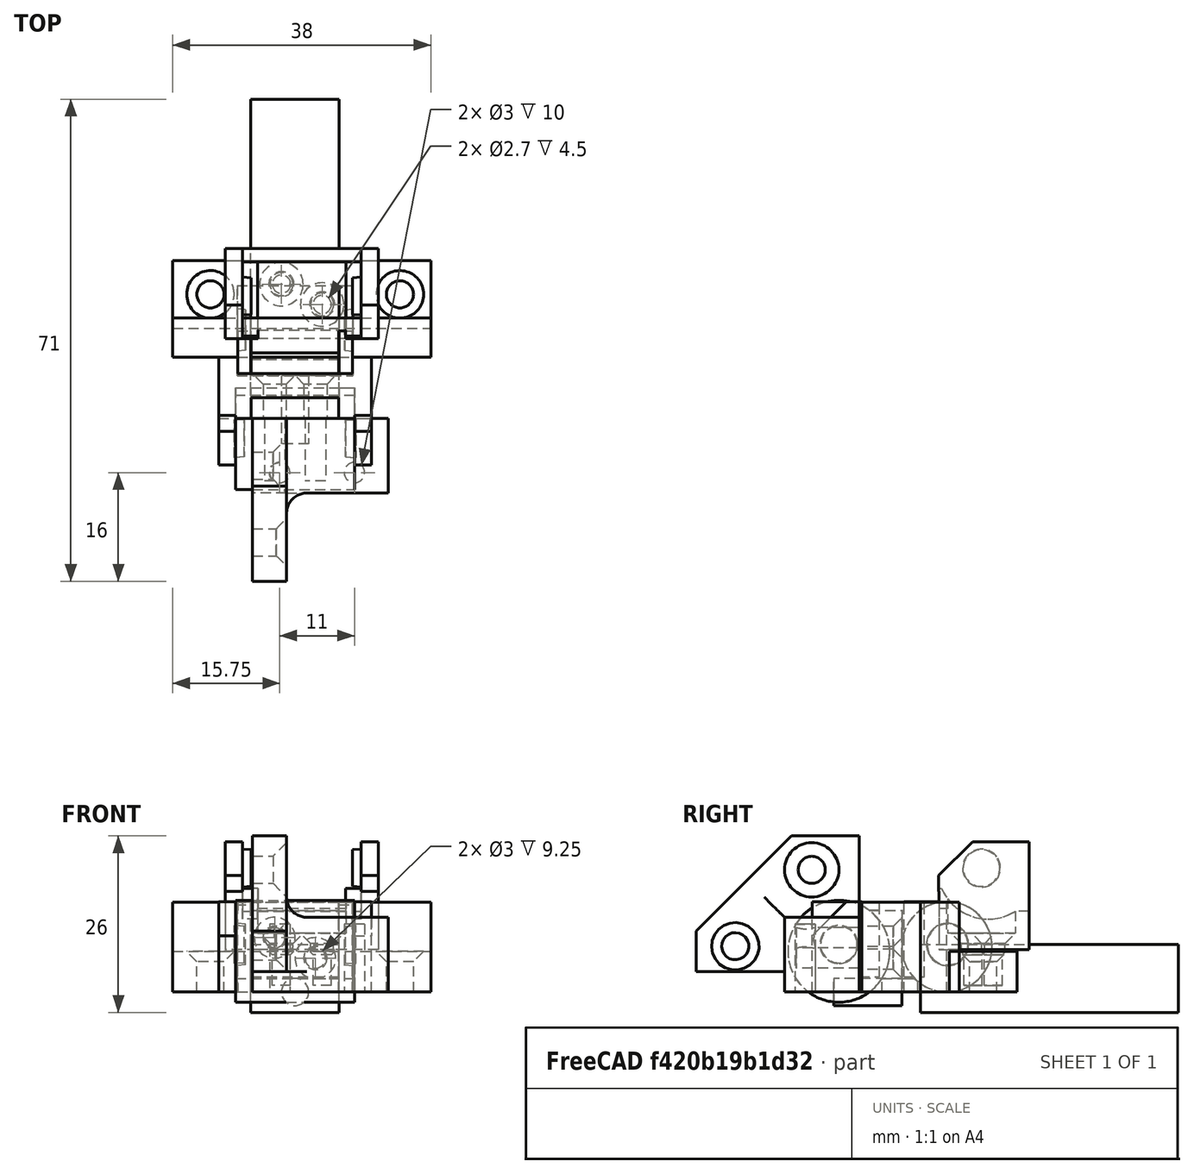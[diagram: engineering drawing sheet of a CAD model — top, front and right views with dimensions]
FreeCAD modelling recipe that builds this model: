
FCSTD DOCUMENT  (FreeCAD 0.18R16146 (Git))
Label: Cable Chain 0.1
License: All rights reserved
LicenseURL: http://en.wikipedia.org/wiki/All_rights_reserved
objects: Part::Box×39, Part::MultiFuse×31, Part::Cut×22, Part::Cylinder×21, Part::Cone×12, Part::Chamfer×9, Part::Mirroring×6, Part::Fuse×3, Mesh::Feature×2, Part::Fillet×2, App::DocumentObjectGroup×1
note: 145 computed .brp shape members not serialized (recipe doc carries the construction recipe); baked Part::Feature solids carry a one-line shape summary decoded from their .brp

FEATURE [Mesh::Feature] CableChain  label="Original STL From Thingiverse"
FEATURE [Part::Box] Box  label="Main Body"
  AttacherType = Attacher::AttachEngine3D
  Height = 13.25
  Length = 22.5
  Placement = pos=(-11.25,-6.25,0) rot=(0,0,1;0rad)
  Width = 9
FEATURE [Part::Cylinder] Cylinder  label="Bump Cylinder"
  Angle = 360
  AttacherType = Attacher::AttachEngine3D
  Height = 17.5
  Placement = pos=(-8.75,-9.25,6) rot=(0,1,0;1.5708rad)
  Radius = 7.5
FEATURE [Part::Cylinder] Cylinder001  label="Dent Cylinder"
  Angle = 360
  AttacherType = Attacher::AttachEngine3D
  Height = 17
  Placement = pos=(-8.5,6.65,6.65) rot=(0,1,0;1.5708rad)
  Radius = 6.65
FEATURE [Part::Box] Box001  label="Cube001"
  AttacherType = Attacher::AttachEngine3D
  Height = 13.3
  Length = 2
  Placement = pos=(6.45,0.35,0) rot=(0,0,1;0rad)
  Width = 6.3
FEATURE [Part::Cone] Cone
  Angle = 360
  AttacherType = Attacher::AttachEngine3D
  Height = 1.2
  Placement = pos=(7.3,6.75,7) rot=(0,1,0;1.5708rad)
  Radius1 = 3
  Radius2 = 3.1
FEATURE [Part::Box] Box002  label="Cube002"
  AttacherType = Attacher::AttachEngine3D
  Height = 13.3
  Length = 2
  Placement = pos=(-8.45,0.35,0) rot=(0,0,1;0rad)
  Width = 6.3
FEATURE [Part::Cone] Cone001
  Angle = 360
  AttacherType = Attacher::AttachEngine3D
  Height = 1.2
  Placement = pos=(7.3,6.75,7) rot=(0,1,0;1.5708rad)
  Radius1 = 3
  Radius2 = 3.1
FEATURE [Part::Mirroring] Part__Mirroring  label="Cone001 (Mirror #1)"
  Base = (0,0,0)
  Normal = (1,0,0)
  Source = -> Cone001
FEATURE [Part::Cone] Cone002
  Angle = 360
  AttacherType = Attacher::AttachEngine3D
  Height = 1.5
  Placement = pos=(7.45,-9.25,7) rot=(0,1,0;1.5708rad)
  Radius1 = 2.7
  Radius2 = 2.8
FEATURE [Part::Box] Box003  label="Cube003"
  AttacherType = Attacher::AttachEngine3D
  Height = 11
  Length = 12.9
  Placement = pos=(-6.45,0.35,2.25) rot=(0,0,1;0rad)
  Width = 3
FEATURE [Part::Box] Box004  label="Cube004"
  AttacherType = Attacher::AttachEngine3D
  Height = 11
  Length = 12.9
  Placement = pos=(-6.45,-6.25,2.25) rot=(0,0,1;0rad)
  Width = 3
FEATURE [Part::Box] Box005  label="Cable Hole"
  AttacherType = Attacher::AttachEngine3D
  Height = 10
  Length = 13
  Placement = pos=(-6.5,-19,2) rot=(0,0,1;0rad)
  Width = 38
FEATURE [Part::Box] Box006  label="Cube006"
  AttacherType = Attacher::AttachEngine3D
  Height = 13.3
  Length = 2.5
  Placement = pos=(8.75,-13.15,0) rot=(0,0,1;0rad)
  Width = 7.3
FEATURE [Part::Box] Box007  label="Cube007"
  AttacherType = Attacher::AttachEngine3D
  Height = 13.3
  Length = 2.5
  Placement = pos=(-11.25,-13.15,0) rot=(0,0,1;0rad)
  Width = 7.3
FEATURE [Part::Cone] Cone003
  Angle = 360
  AttacherType = Attacher::AttachEngine3D
  Height = 1.5
  Placement = pos=(7.45,-9.25,7) rot=(0,1,0;1.5708rad)
  Radius1 = 2.7
  Radius2 = 2.8
FEATURE [Part::Mirroring] Part__Mirroring001  label="Cone003 (Mirror #2)"
  Base = (0,0,0)
  Normal = (1,0,0)
  Source = -> Cone003
FEATURE [Part::MultiFuse] Fusion  label="Dent Cubes"
  Shapes = -> [Box001,Box002]
FEATURE [Part::MultiFuse] Fusion001  label="Bump Cubes"
  Shapes = -> [Box006,Box007]
FEATURE [Part::MultiFuse] Fusion002  label="Dents"
  Shapes = -> [Cone,Part__Mirroring]
FEATURE [Part::MultiFuse] Fusion003  label="Bumps"
  Shapes = -> [Part__Mirroring001,Cone002]
FEATURE [Mesh::Feature] CableChain001  label="Copy of Original STL"
  Placement = pos=(25,0,0) rot=(0,0,1;0rad)
FEATURE [Part::MultiFuse] Fusion004
  Shapes = -> [Box,Fusion]
FEATURE [Part::MultiFuse] Fusion005
  Shapes = -> [Fusion004,Fusion001]
FEATURE [Part::MultiFuse] Fusion006
  Shapes = -> [Cylinder001,Fusion005]
FEATURE [Part::Cut] Cut
  Base = -> Fusion006
  Tool = -> Cylinder
FEATURE [Part::MultiFuse] Fusion007
  Shapes = -> [Box003,Box004]
FEATURE [Part::Cut] Cut001
  Base = -> Cut
  Tool = -> Fusion007
FEATURE [Part::Cut] Cut002
  Base = -> Cut001
  Tool = -> Box005
FEATURE [Part::Box] Box008  label="Cube"
  AttacherType = Attacher::AttachEngine3D
  Height = 18
  Length = 13
  Placement = pos=(-6.5,0.35,2) rot=(0,0,1;0rad)
  Width = 13
FEATURE [Part::Cut] Cut003
  Base = -> Cut002
  Tool = -> Box008
FEATURE [Part::Box] Box009  label="Cube008"
  AttacherType = Attacher::AttachEngine3D
  Height = 10
  Length = 17.5
  Placement = pos=(-8.75,-10.91,-1) rot=(0,0,1;0rad)
  Width = 8
FEATURE [Part::Cut] Cut004
  Base = -> Cut003
  Tool = -> Box009
FEATURE [Part::Box] Box010  label="Cable Hole001"
  AttacherType = Attacher::AttachEngine3D
  Height = 10
  Length = 13
  Placement = pos=(-6.5,2.75,-3) rot=(0,0,1;0rad)
  Width = 38
FEATURE [Part::Cut] Cut005
  Base = -> Cut004
  Tool = -> Box010
FEATURE [Part::Chamfer] Chamfer
  Base = -> Cut005
  Edges = 2 edges r=5: [Edge192,Edge198]
FEATURE [Part::Fuse] Fusion008
  Base = -> Fusion003
  Tool = -> Chamfer
FEATURE [Part::Cut] Cut006  label="Cable Chain 0.1"
  Base = -> Fusion008
  Tool = -> Fusion002
FEATURE [Part::Cylinder] Cylinder006
  Angle = 360
  AttacherType = Attacher::AttachEngine3D
  Height = 10
  Placement = pos=(3,7,5) rot=(1,0,0;1.5708rad)
  Radius = 1.7
FEATURE [Part::Box] Box011  label="Main Body001"
  AttacherType = Attacher::AttachEngine3D
  Height = 13.25
  Length = 22.5
  Placement = pos=(-11.25,-6.25,0) rot=(0,0,1;0rad)
  Width = 9
FEATURE [Part::Cylinder] Cylinder008  label="Bump Cylinder001"
  Angle = 360
  AttacherType = Attacher::AttachEngine3D
  Height = 17.5
  Placement = pos=(-8.75,-9.25,6) rot=(0,1,0;1.5708rad)
  Radius = 7.5
FEATURE [Part::Box] Box012  label="Cube009"
  AttacherType = Attacher::AttachEngine3D
  Height = 13.3
  Length = 2
  Placement = pos=(6.45,0.35,0) rot=(0,0,1;0rad)
  Width = 6.3
FEATURE [Part::Cylinder] Cylinder009  label="Dent Cylinder001"
  Angle = 360
  AttacherType = Attacher::AttachEngine3D
  Height = 17
  Placement = pos=(-8.5,6.65,6.65) rot=(0,1,0;1.5708rad)
  Radius = 6.65
FEATURE [Part::Cone] Cone004
  Angle = 360
  AttacherType = Attacher::AttachEngine3D
  Height = 1.2
  Placement = pos=(7.3,6.75,7) rot=(0,1,0;1.5708rad)
  Radius1 = 3
  Radius2 = 3.1
FEATURE [Part::Box] Box013  label="Cube010"
  AttacherType = Attacher::AttachEngine3D
  Height = 13.3
  Length = 2
  Placement = pos=(-8.45,0.35,0) rot=(0,0,1;0rad)
  Width = 6.3
FEATURE [Part::Cone] Cone005
  Angle = 360
  AttacherType = Attacher::AttachEngine3D
  Height = 1.2
  Placement = pos=(7.3,6.75,7) rot=(0,1,0;1.5708rad)
  Radius1 = 3
  Radius2 = 3.1
FEATURE [Part::Mirroring] Part__Mirroring002  label="Cone001 (Mirror #1)001"
  Base = (0,0,0)
  Normal = (1,0,0)
  Source = -> Cone005
FEATURE [Part::Box] Box014  label="Cube011"
  AttacherType = Attacher::AttachEngine3D
  Height = 11
  Length = 12.9
  Placement = pos=(-6.45,0.35,2.25) rot=(0,0,1;0rad)
  Width = 3
FEATURE [Part::Cone] Cone006
  Angle = 360
  AttacherType = Attacher::AttachEngine3D
  Height = 1.5
  Placement = pos=(7.45,-9.25,7) rot=(0,1,0;1.5708rad)
  Radius1 = 2.7
  Radius2 = 2.8
FEATURE [Part::Box] Box015  label="Cube012"
  AttacherType = Attacher::AttachEngine3D
  Height = 11
  Length = 12.9
  Placement = pos=(-6.45,-6.25,2.25) rot=(0,0,1;0rad)
  Width = 3
FEATURE [Part::Box] Box016  label="Cable Hole002"
  AttacherType = Attacher::AttachEngine3D
  Height = 10
  Length = 13
  Placement = pos=(-6.5,-19,2) rot=(0,0,1;0rad)
  Width = 38
FEATURE [Part::Box] Box017  label="Cube013"
  AttacherType = Attacher::AttachEngine3D
  Height = 13.3
  Length = 2.5
  Placement = pos=(8.75,-13.15,0) rot=(0,0,1;0rad)
  Width = 7.3
FEATURE [Part::Box] Box018  label="Cube014"
  AttacherType = Attacher::AttachEngine3D
  Height = 13.3
  Length = 2.5
  Placement = pos=(-11.25,-13.15,0) rot=(0,0,1;0rad)
  Width = 7.3
FEATURE [Part::Cone] Cone007
  Angle = 360
  AttacherType = Attacher::AttachEngine3D
  Height = 1.5
  Placement = pos=(7.45,-9.25,7) rot=(0,1,0;1.5708rad)
  Radius1 = 2.7
  Radius2 = 2.8
FEATURE [Part::Mirroring] Part__Mirroring003  label="Cone003 (Mirror #2)001"
  Base = (0,0,0)
  Normal = (1,0,0)
  Source = -> Cone007
FEATURE [Part::MultiFuse] Fusion009  label="Dent Cubes001"
  Shapes = -> [Box012,Box013]
FEATURE [Part::MultiFuse] Fusion010  label="Bump Cubes001"
  Shapes = -> [Box017,Box018]
FEATURE [Part::MultiFuse] Fusion011  label="Dents001"
  Shapes = -> [Cone004,Part__Mirroring002]
FEATURE [Part::MultiFuse] Fusion012  label="Bumps001"
  Shapes = -> [Part__Mirroring003,Cone006]
FEATURE [Part::MultiFuse] Fusion016
  Shapes = -> [Box014,Box015]
FEATURE [Part::Box] Box019  label="Cube015"
  AttacherType = Attacher::AttachEngine3D
  Height = 18
  Length = 13
  Placement = pos=(-6.5,0.35,2) rot=(0,0,1;0rad)
  Width = 13
FEATURE [Part::Box] Box020  label="Cube016"
  AttacherType = Attacher::AttachEngine3D
  Height = 10
  Length = 17.5
  Placement = pos=(-8.75,-10.91,-1) rot=(0,0,1;0rad)
  Width = 8
FEATURE [Part::Box] Box021  label="Cable Hole003"
  AttacherType = Attacher::AttachEngine3D
  Height = 10
  Length = 13
  Placement = pos=(-6.5,2.75,-3) rot=(0,0,1;0rad)
  Width = 38
FEATURE [Part::Box] Box022  label="Cube017"
  AttacherType = Attacher::AttachEngine3D
  Height = 12
  Length = 22.5
  Placement = pos=(-11.25,0.35,1.25) rot=(0,0,1;0rad)
  Width = 2.4
FEATURE [Part::Cylinder] Cylinder004
  Angle = 360
  AttacherType = Attacher::AttachEngine3D
  Height = 10
  Placement = pos=(26.45,12,-8) rot=(0,0,1;0rad)
  Radius = 2
FEATURE [Part::Cylinder] Cylinder005
  Angle = 360
  AttacherType = Attacher::AttachEngine3D
  Height = 10
  Placement = pos=(-1.45,12,-8) rot=(0,0,1;0rad)
  Radius = 2
FEATURE [Part::Box] Box023  label="Cube018"
  AttacherType = Attacher::AttachEngine3D
  Height = 6
  Length = 38
  Placement = pos=(-7,7,-5) rot=(0,0,1;0rad)
  Width = 10
FEATURE [Part::MultiFuse] Fusion019
  Shapes = -> [Cylinder004,Cylinder005]
FEATURE [Part::Cut] Cut014
  Base = -> Box023
  Placement = pos=(-11,0,5) rot=(0,0,1;0rad)
  Tool = -> Fusion019
FEATURE [Part::MultiFuse] Fusion021
  Shapes = -> [Box011,Fusion010]
FEATURE [Part::Cut] Cut016
  Base = -> Fusion021
  Tool = -> Cylinder008
FEATURE [Part::Cut] Cut017
  Base = -> Cut016
  Tool = -> Box016
FEATURE [Part::Cut] Cut018
  Base = -> Cut017
  Tool = -> Fusion016
FEATURE [Part::MultiFuse] Fusion022
  Shapes = -> [Box019,Box020,Box021]
FEATURE [Part::Cut] Cut019
  Base = -> Cut018
  Tool = -> Fusion022
FEATURE [Part::MultiFuse] Fusion023
  Shapes = -> [Cut019,Fusion012]
FEATURE [Part::Cylinder] Cylinder010
  Angle = 360
  AttacherType = Attacher::AttachEngine3D
  Height = 10
  Placement = pos=(-3,7,8) rot=(1,0,0;1.5708rad)
  Radius = 1.7
FEATURE [Part::MultiFuse] Fusion024
  Shapes = -> [Cylinder006,Cylinder010]
FEATURE [Part::MultiFuse] Fusion025
  Placement = pos=(-1e-15,0,13.25) rot=(0,1,0;3.14159rad)
  Shapes = -> [Fusion023,Box022]
FEATURE [Part::Box] Box024  label="Cube019"
  AttacherType = Attacher::AttachEngine3D
  Height = 13.25
  Length = 38
  Placement = pos=(-18,2.75,0) rot=(0,0,1;0rad)
  Width = 5.75
FEATURE [Part::Cylinder] Cylinder011
  Angle = 360
  AttacherType = Attacher::AttachEngine3D
  Height = 10
  Placement = pos=(-2,13.5,1) rot=(1,0,0;0rad)
  Radius = 1.35
FEATURE [Part::Cylinder] Cylinder012
  Angle = 360
  AttacherType = Attacher::AttachEngine3D
  Height = 10
  Placement = pos=(4,10.5,1) rot=(1,0,0;0rad)
  Radius = 1.35
FEATURE [Part::MultiFuse] Fusion027
  Shapes = -> [Cylinder011,Cylinder012]
FEATURE [Part::Cylinder] Cylinder013  label="Cylinder"
  Angle = 360
  AttacherType = Attacher::AttachEngine3D
  Height = 10
  Placement = pos=(0,0,0) rot=(1,0,0;1.5708rad)
  Radius = 2
FEATURE [Part::Cut] Cut020
  Base = -> Fusion025
  Tool = -> Fusion024
FEATURE [Part::Chamfer] Chamfer008
  Base = -> Cut020
  Edges = 2 edges r=1.5: [Edge88,Edge90]
FEATURE [Part::Chamfer] Chamfer009  label="Electronics Cable End 0.1"
  Base = -> Chamfer008
  Edges = 2 edges r=5: [Edge138,Edge148]
  Placement = pos=(1,5.5,9) rot=(-1,0,0;1.5708rad)
FEATURE [Part::Cut] Cut021
  Base = -> Cut014
  Tool = -> Fusion027
FEATURE [Part::Chamfer] Chamfer010  label="Electronics End Mount 0.1"
  Base = -> Cut021
  Edges = 2 edges r=1.5: [Edge10,Edge13]
FEATURE [Part::Cylinder] Cylinder014
  Angle = 360
  AttacherType = Attacher::AttachEngine3D
  Height = 10
  Placement = pos=(0,214,-16) rot=(0,1,0;1.5708rad)
  Radius = 2
FEATURE [Part::Box] Box025  label="Cube022"
  AttacherType = Attacher::AttachEngine3D
  Height = 20
  Length = 5
  Placement = pos=(3,207,-21) rot=(0,0,1;0rad)
  Width = 24
FEATURE [Part::Cylinder] Cylinder015
  Angle = 360
  AttacherType = Attacher::AttachEngine3D
  Height = 10
  Placement = pos=(0,225.25,-4.75) rot=(0.357407,0.862856,0.357407;1.71777rad)
  Radius = 2
FEATURE [Part::Box] Box026  label="Cube023"
  AttacherType = Attacher::AttachEngine3D
  Height = 11
  Length = 20
  Placement = pos=(3,207,-9) rot=(0,0,1;0rad)
  Width = 11
FEATURE [Part::Cylinder] Cylinder016
  Angle = 360
  AttacherType = Attacher::AttachEngine3D
  Height = 10
  Placement = pos=(18,215,-8) rot=(0,0,1;0rad)
  Radius = 1.5
FEATURE [Part::Cylinder] Cylinder017
  Angle = 360
  AttacherType = Attacher::AttachEngine3D
  Height = 14
  Placement = pos=(7,215,-8) rot=(0,0,1;0rad)
  Radius = 1.5
FEATURE [Part::Fuse] Fusion028
  Base = -> Box025
  Tool = -> Box026
FEATURE [Part::MultiFuse] Fusion029
  Shapes = -> [Cylinder015,Cylinder014]
FEATURE [Part::MultiFuse] Fusion013
  Shapes = -> [Cylinder017,Cylinder016]
FEATURE [Part::Fillet] Fillet002
  Base = -> Fusion028
  Edges = 1 edges r=3: [Edge18]
FEATURE [Part::Fillet] Fillet003
  Base = -> Fillet002
  Edges = 1 edges r=3: [Edge10]
FEATURE [Part::Cut] Cut022
  Base = -> Fillet003
  Tool = -> Fusion013
FEATURE [Part::Cut] Cut023
  Base = -> Cut022
  Tool = -> Fusion029
FEATURE [Part::Chamfer] Chamfer015
  Base = -> Cut023
  Edges = 1 edges r=1.5: [Edge9]
FEATURE [Part::Chamfer] Chamfer016  label="chamf16"
  Base = -> Chamfer015
  Edges = 1 edges r=2: [Edge10]
FEATURE [Part::Chamfer] Chamfer017  label="cable chain mount bed end 0.2"
  Base = -> Chamfer016
  Edges = 1 edges r=14: [Edge22]
  Placement = pos=(-9.25,200.75,2) rot=(1,0,0;3.14159rad)
FEATURE [Part::Box] Box027  label="Main Body002"
  AttacherType = Attacher::AttachEngine3D
  Height = 13.25
  Length = 22.5
  Placement = pos=(-11.25,-6.25,0) rot=(0,0,1;0rad)
  Width = 9
FEATURE [Part::Cylinder] Cylinder018  label="Bump Cylinder002"
  Angle = 360
  AttacherType = Attacher::AttachEngine3D
  Height = 17.5
  Placement = pos=(-8.75,-9.25,6) rot=(0,1,0;1.5708rad)
  Radius = 7.5
FEATURE [Part::Cylinder] Cylinder019  label="Dent Cylinder002"
  Angle = 360
  AttacherType = Attacher::AttachEngine3D
  Height = 17
  Placement = pos=(-8.5,6.65,6.65) rot=(0,1,0;1.5708rad)
  Radius = 6.65
FEATURE [Part::Box] Box028  label="Cube024"
  AttacherType = Attacher::AttachEngine3D
  Height = 13.3
  Length = 2
  Placement = pos=(6.45,0.35,0) rot=(0,0,1;0rad)
  Width = 6.3
FEATURE [Part::Cone] Cone008
  Angle = 360
  AttacherType = Attacher::AttachEngine3D
  Height = 1.2
  Placement = pos=(7.3,6.75,7) rot=(0,1,0;1.5708rad)
  Radius1 = 3
  Radius2 = 3.1
FEATURE [Part::Cone] Cone009
  Angle = 360
  AttacherType = Attacher::AttachEngine3D
  Height = 1.2
  Placement = pos=(7.3,6.75,7) rot=(0,1,0;1.5708rad)
  Radius1 = 3
  Radius2 = 3.1
FEATURE [Part::Box] Box029  label="Cube025"
  AttacherType = Attacher::AttachEngine3D
  Height = 13.3
  Length = 2
  Placement = pos=(-8.45,0.35,0) rot=(0,0,1;0rad)
  Width = 6.3
FEATURE [Part::Mirroring] Part__Mirroring004  label="Cone001 (Mirror #1)002"
  Base = (0,0,0)
  Normal = (1,0,0)
  Source = -> Cone009
FEATURE [Part::Cone] Cone010
  Angle = 360
  AttacherType = Attacher::AttachEngine3D
  Height = 1.5
  Placement = pos=(7.45,-9.25,7) rot=(0,1,0;1.5708rad)
  Radius1 = 2.7
  Radius2 = 2.8
FEATURE [Part::Box] Box030  label="Cube026"
  AttacherType = Attacher::AttachEngine3D
  Height = 11
  Length = 12.9
  Placement = pos=(-6.45,0.35,2.25) rot=(0,0,1;0rad)
  Width = 3
FEATURE [Part::Box] Box031  label="Cube027"
  AttacherType = Attacher::AttachEngine3D
  Height = 11
  Length = 12.9
  Placement = pos=(-6.45,-6.25,2.25) rot=(0,0,1;0rad)
  Width = 3
FEATURE [Part::Box] Box032  label="Cable Hole004"
  AttacherType = Attacher::AttachEngine3D
  Height = 10
  Length = 13
  Placement = pos=(-6.5,-19,2) rot=(0,0,1;0rad)
  Width = 38
FEATURE [Part::Box] Box033  label="Cube028"
  AttacherType = Attacher::AttachEngine3D
  Height = 13.3
  Length = 2.5
  Placement = pos=(8.75,-13.15,0) rot=(0,0,1;0rad)
  Width = 7.3
FEATURE [Part::Box] Box034  label="Cube029"
  AttacherType = Attacher::AttachEngine3D
  Height = 13.3
  Length = 2.5
  Placement = pos=(-11.25,-13.15,0) rot=(0,0,1;0rad)
  Width = 7.3
FEATURE [Part::Cone] Cone011
  Angle = 360
  AttacherType = Attacher::AttachEngine3D
  Height = 1.5
  Placement = pos=(7.45,-9.25,7) rot=(0,1,0;1.5708rad)
  Radius1 = 2.7
  Radius2 = 2.8
FEATURE [Part::Mirroring] Part__Mirroring005  label="Cone003 (Mirror #2)002"
  Base = (0,0,0)
  Normal = (1,0,0)
  Source = -> Cone011
FEATURE [Part::MultiFuse] Fusion030  label="Dent Cubes002"
  Shapes = -> [Box028,Box029]
FEATURE [Part::MultiFuse] Fusion031  label="Bump Cubes002"
  Shapes = -> [Box033,Box034]
FEATURE [Part::MultiFuse] Fusion032  label="Dents002"
  Shapes = -> [Cone008,Part__Mirroring004]
FEATURE [Part::MultiFuse] Fusion033  label="Bumps002"
  Shapes = -> [Part__Mirroring005,Cone010]
FEATURE [Part::MultiFuse] Fusion034
  Shapes = -> [Box027,Fusion030]
FEATURE [Part::MultiFuse] Fusion037
  Shapes = -> [Box030,Box031]
FEATURE [Part::Box] Box035  label="Cube030"
  AttacherType = Attacher::AttachEngine3D
  Height = 18
  Length = 13
  Placement = pos=(-6.5,0.35,2) rot=(0,0,1;0rad)
  Width = 13
FEATURE [Part::Box] Box036  label="Cube031"
  AttacherType = Attacher::AttachEngine3D
  Height = 13
  Length = 18.5
  Placement = pos=(-8.75,-6.25,0) rot=(0,0,1;0rad)
  Width = 6.3
FEATURE [Part::Box] Box037  label="Cable Hole005"
  AttacherType = Attacher::AttachEngine3D
  Height = 10
  Length = 13
  Placement = pos=(-6.5,2.75,-3) rot=(0,0,1;0rad)
  Width = 38
FEATURE [App::DocumentObjectGroup] Group  label="Unused copies etc"
  Group = -> [Cylinder009,Fusion009,Fusion011,Box024,Fusion033,Cylinder018,Fusion031,Box037,Fusion037]
FEATURE [Part::Fuse] Fusion038
  Base = -> Cylinder019
  Tool = -> Fusion034
FEATURE [Part::Cut] Cut024
  Base = -> Fusion038
  Tool = -> Box032
FEATURE [Part::Cut] Cut025
  Base = -> Cut024
  Tool = -> Box035
FEATURE [Part::Box] Box038  label="Cube032"
  AttacherType = Attacher::AttachEngine3D
  Height = 18
  Length = 13
  Placement = pos=(-6.5,2.35,-3) rot=(0,0,1;0rad)
  Width = 13
FEATURE [Part::Cut] Cut026
  Base = -> Cut025
  Tool = -> Box038
FEATURE [Part::Cylinder] Cylinder020
  Angle = 360
  AttacherType = Attacher::AttachEngine3D
  Height = 10
  Placement = pos=(3,-5.5,5) rot=(1,0,0;1.5708rad)
  Radius = 1.5
FEATURE [Part::Cylinder] Cylinder021
  Angle = 360
  AttacherType = Attacher::AttachEngine3D
  Height = 10
  Placement = pos=(-3,-5.5,8) rot=(1,0,0;1.5708rad)
  Radius = 1.5
FEATURE [Part::Cylinder] Cylinder022
  Angle = 360
  AttacherType = Attacher::AttachEngine3D
  Height = 10
  Placement = pos=(3,2,5) rot=(1,0,0;1.5708rad)
  Radius = 1.7
FEATURE [Part::Cylinder] Cylinder023
  Angle = 360
  AttacherType = Attacher::AttachEngine3D
  Height = 10
  Placement = pos=(-3,2,8) rot=(1,0,0;1.5708rad)
  Radius = 1.7
FEATURE [Part::MultiFuse] Fusion039
  Shapes = -> [Box036,Cut026]
FEATURE [Part::MultiFuse] Fusion040
  Shapes = -> [Cylinder023,Cylinder022]
FEATURE [Part::Cut] Cut027
  Base = -> Fusion039
  Tool = -> Fusion040
FEATURE [Part::Cut] Cut028  label="Bed Cable End 0.1"
  Base = -> Cut027
  Tool = -> Fusion032
FEATURE [Part::MultiFuse] Fusion041
  Shapes = -> [Cylinder020,Cylinder021]
FEATURE [Part::Cut] Cut029  label="Bed End Mount 0.1"
  Base = -> Chamfer017
  Tool = -> Fusion041
FEATURE [Part::Chamfer] Chamfer018  label="Bed Cable End 0.1."
  Base = -> Cut028
  Edges = 2 edges r=1.3: [Edge44,Edge46]
FEATURE [Part::Chamfer] Chamfer019  label="Electronics End Mount with Chamfer 0.1"
  Base = -> Chamfer010
  Edges = 2 edges r=0.5: [Edge6,Edge7]
